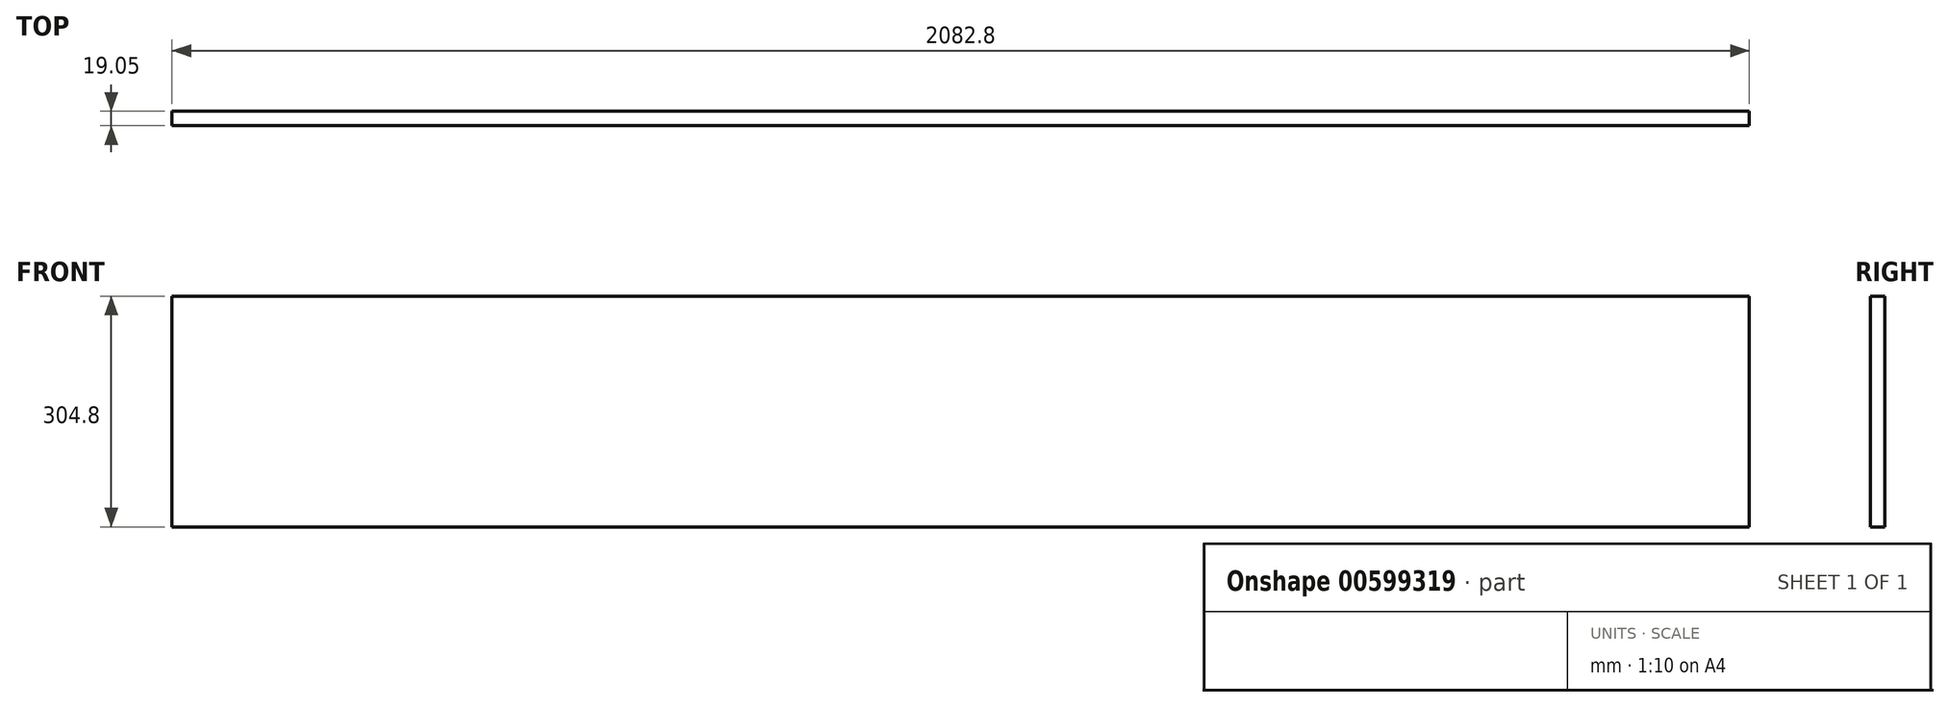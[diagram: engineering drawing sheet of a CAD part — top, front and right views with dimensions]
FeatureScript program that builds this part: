
annotation { "Feature Type Name" : "Feature", "Feature Type Description" : "" }
export const myFeature = defineFeature(function(context is Context, id is Id, definition is map)
    precondition{}
    {
        {
            var Q0;
            Q0=qCreatedBy(makeId("Front.planeOp"),FACE);
            var sketch = newSketch(context, id + "F0", { "sketchPlane" : qUnion([Q0])});
            skLineSegment(sketch, "E0.bottom", {"start": v(-304.22, 202.66) * mm, "end": v(1778.58, 202.66) * mm});
            skLineSegment(sketch, "E0.top", {"start": v(-304.22, -102.14) * mm, "end": v(1778.58, -102.14) * mm});
            skLineSegment(sketch, "E0.left", {"start": v(-304.22, 202.66) * mm, "end": v(-304.22, -102.14) * mm});
            skLineSegment(sketch, "E0.right", {"start": v(1778.58, 202.66) * mm, "end": v(1778.58, -102.14) * mm});
            skSolve(sketch);
        }
        {
            var Q0;
            Q0=makeQuery(id+"F0.imprint","IMPRINT",FACE,{"disambiguationData":[TD([[makeQuery(id+"F0.imprint","IMPRINT",EDGE,{"derivedFrom":sQuery(id+"F0.wireOp",EDGE,"E0.bottom")}),-1.0]])]});
            extrude(context, id + "F1", {"entities" : qUnion([Q0]), "depth" : 19.05 * mm, "offsetDistance" : 25.4 * mm});
        }
    });
